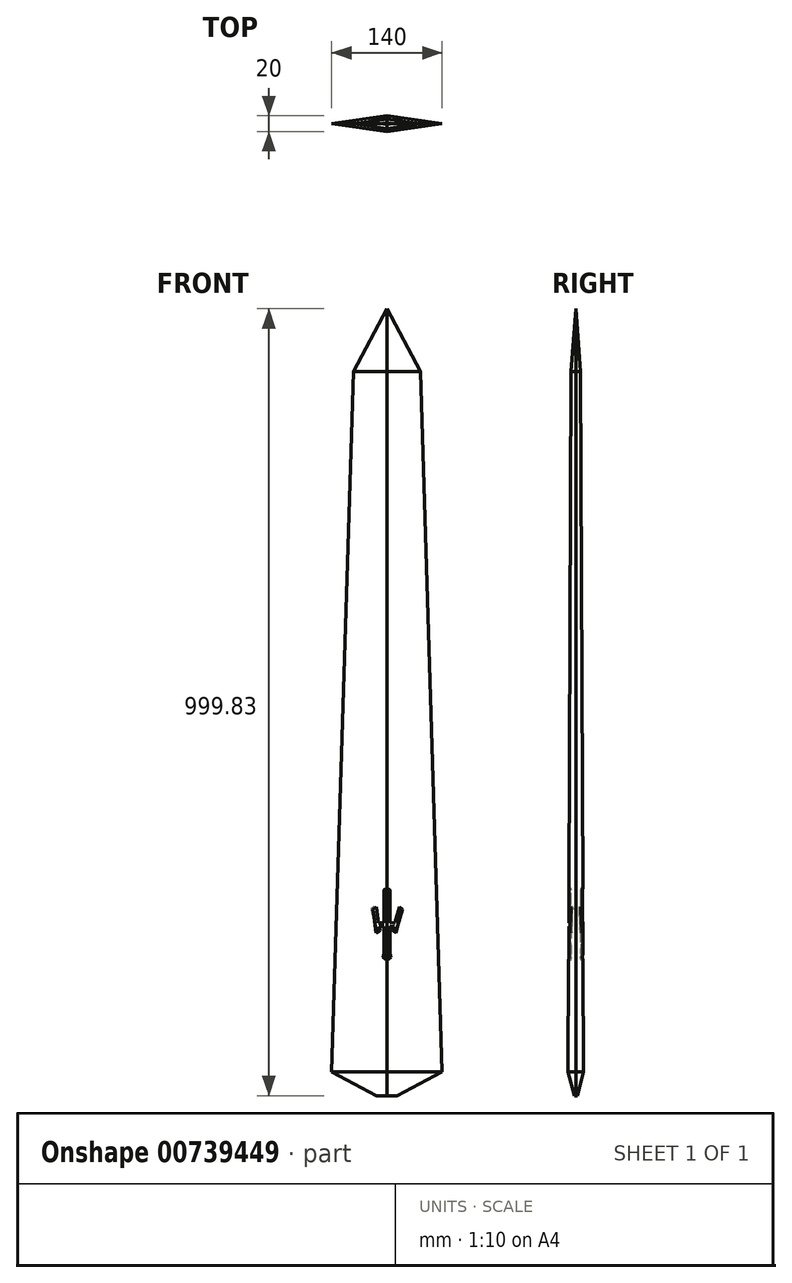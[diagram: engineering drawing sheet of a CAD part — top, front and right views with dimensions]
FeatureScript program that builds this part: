
annotation { "Feature Type Name" : "Feature", "Feature Type Description" : "" }
export const myFeature = defineFeature(function(context is Context, id is Id, definition is map)
    precondition{}
    {
        {
            var Q0;
            Q0=qCreatedBy(makeId("Top.planeOp"),FACE);
            var sketch = newSketch(context, id + "F0", { "sketchPlane" : qUnion([Q0])});
            skLineSegment(sketch, "E0", {"start": v(0, 0) * mm, "end": v(-70, 0) * mm});
            skLineSegment(sketch, "E1", {"start": v(0, 0) * mm, "end": v(70, 0) * mm});
            skLineSegment(sketch, "E2", {"start": v(0, 0) * mm, "end": v(0, 10) * mm});
            skLineSegment(sketch, "E3", {"start": v(0, 0) * mm, "end": v(0, -10) * mm});
            skLineSegment(sketch, "E4", {"start": v(-70, 0) * mm, "end": v(0, 10) * mm});
            skLineSegment(sketch, "E5", {"start": v(70, 0) * mm, "end": v(0, 10) * mm});
            skLineSegment(sketch, "E6", {"start": v(-70, 0) * mm, "end": v(0, -10) * mm});
            skLineSegment(sketch, "E7", {"start": v(70, 0) * mm, "end": v(0, -10) * mm});
            skSolve(sketch);
        }
        {
            var Q0;
            Q0=makeQuery(id+"F0.imprint","IMPRINT",FACE,{"disambiguationData":[TD([[makeQuery(id+"F0.imprint","IMPRINT",EDGE,{"derivedFrom":sQuery(id+"F0.wireOp",EDGE,"E0")}),-1.0]])]});
            var Q1;
            Q1=makeQuery(id+"F0.imprint","IMPRINT",FACE,{"disambiguationData":[TD([[makeQuery(id+"F0.imprint","IMPRINT",EDGE,{"derivedFrom":sQuery(id+"F0.wireOp",EDGE,"E0")}),1.0]])]});
            var Q2;
            Q2=makeQuery(id+"F0.imprint","IMPRINT",FACE,{"disambiguationData":[TD([[makeQuery(id+"F0.imprint","IMPRINT",EDGE,{"derivedFrom":sQuery(id+"F0.wireOp",EDGE,"E1")}),1.0]])]});
            var Q3;
            Q3=makeQuery(id+"F0.imprint","IMPRINT",FACE,{"disambiguationData":[TD([[makeQuery(id+"F0.imprint","IMPRINT",EDGE,{"derivedFrom":sQuery(id+"F0.wireOp",EDGE,"E1")}),-1.0]])]});
            extrude(context, id + "F1", {"entities" : qUnion([Q0, Q1, Q2, Q3]), "depth" : 890 * mm, "offsetDistance" : 25 * mm, "hasDraft" : true, "draftAngle" : .25 * degree, "draftPullDirection" : true});
        }
        {
            var Q0;
            Q0=makeQuery(id+"F1.opExtrude","CAP_FACE",FACE,{"disambiguationData":[OSD([sQuery(id+"F0.wireOp",EDGE,"E4"),sQuery(id+"F0.wireOp",EDGE,"E5"),sQuery(id+"F0.wireOp",EDGE,"E6"),sQuery(id+"F0.wireOp",EDGE,"E7")])],"isStart":false});
            var sketch = newSketch(context, id + "F2", { "sketchPlane" : qUnion([Q0])});
            skSolve(sketch);
        }
        {
            var Q0;
            Q0 = qSketchRegion(id + "F2", true);
            var Q1;
            Q1=makeQuery(id+"F2.imprint","IMPRINT",FACE,{"disambiguationData":[TD([[makeQuery(id+"F2.imprint","IMPRINT",EDGE,{"derivedFrom":makeQuery(id+"F1.opExtrude","CAP_EDGE",EDGE,{"disambiguationData":[OSD([sQuery(id+"F0.wireOp",EDGE,"E4")])],"isStart":false})}),-1.0]])]});
            extrude(context, id + "F3", {"entities" : qUnion([Q0, Q1]), "depth" : 80 * mm, "offsetDistance" : 25 * mm, "hasDraft" : true, "draftAngle" : 4.3 * degree, "draftPullDirection" : true});
        }
        {
            var Q0;
            Q0=makeQuery(id+"F1.opExtrude","CAP_FACE",FACE,{"disambiguationData":[OSD([sQuery(id+"F0.wireOp",EDGE,"E4"),sQuery(id+"F0.wireOp",EDGE,"E5"),sQuery(id+"F0.wireOp",EDGE,"E6"),sQuery(id+"F0.wireOp",EDGE,"E7")])],"isStart":true});
            extrude(context, id + "F4", {"entities" : qUnion([Q0]), "depth" : 30 * mm, "offsetDistance" : 25 * mm, "hasDraft" : true, "draftAngle" : 15 * degree, "draftPullDirection" : true});
        }
        {
            var Q0;
            Q0=makeQuery(id+"F1.opExtrude","SWEPT_FACE",FACE,{"disambiguationData":[OSD([sQuery(id+"F0.wireOp",EDGE,"E6")])]});
            var sketch = newSketch(context, id + "F5", { "sketchPlane" : qUnion([Q0])});
            skLineSegment(sketch, "E8", {"start": v(-2.59, 149.93) * mm, "end": v(1.41, 149.93) * mm});
            skLineSegment(sketch, "E9", {"start": v(-2.59, 231.66) * mm, "end": v(1.41, 231.66) * mm});
            skLineSegment(sketch, "E10", {"start": v(1.41, 231.66) * mm, "end": v(1.41, 149.93) * mm});
            skLineSegment(sketch, "E11", {"start": v(-2.59, 149.93) * mm, "end": v(-2.59, 184.78) * mm});
            skLineSegment(sketch, "E12", {"start": v(-2.59, 184.78) * mm, "end": v(-8.43, 184.78) * mm});
            skLineSegment(sketch, "E13", {"start": v(-8.43, 184.78) * mm, "end": v(-13.43, 184.78) * mm});
            skLineSegment(sketch, "E14", {"start": v(-12.29, 176.83) * mm, "end": v(-13.43, 184.78) * mm});
            skLineSegment(sketch, "E15", {"start": v(-8.43, 184.78) * mm, "end": v(-11.6, 206.86) * mm});
            skLineSegment(sketch, "E16", {"start": v(-13.43, 184.78) * mm, "end": v(-16.6, 206.86) * mm});
            skLineSegment(sketch, "E17", {"start": v(-2.59, 184.78) * mm, "end": v(-2.59, 189.78) * mm});
            skLineSegment(sketch, "E18", {"start": v(-2.59, 189.78) * mm, "end": v(-9.14, 189.78) * mm});
            skLineSegment(sketch, "E19", {"start": v(-2.59, 189.78) * mm, "end": v(-2.59, 231.66) * mm});
            skLineSegment(sketch, "E20", {"start": v(-11.6, 206.86) * mm, "end": v(-12.02, 209.86) * mm});
            skLineSegment(sketch, "E21", {"start": v(-12.02, 209.86) * mm, "end": v(-16.6, 206.86) * mm});
            skLineSegment(sketch, "E22", {"start": v(-7.66, 179.83) * mm, "end": v(-12.29, 176.83) * mm});
            skLineSegment(sketch, "E23", {"start": v(-7.66, 179.83) * mm, "end": v(-8.43, 184.78) * mm});
            skLineSegment(sketch, "E24", {"start": v(1.41, 231.66) * mm, "end": v(1.41, 233.66) * mm});
            skLineSegment(sketch, "E25", {"start": v(1.41, 233.66) * mm, "end": v(-2.59, 231.66) * mm});
            skLineSegment(sketch, "E26", {"start": v(1.41, 149.93) * mm, "end": v(1.41, 141.93) * mm});
            skLineSegment(sketch, "E27", {"start": v(1.41, 145.93) * mm, "end": v(-3.59, 145.93) * mm});
            skLineSegment(sketch, "E28", {"start": v(-3.59, 145.93) * mm, "end": v(-2.59, 149.93) * mm});
            skLineSegment(sketch, "E29", {"start": v(-3.59, 145.93) * mm, "end": v(1.41, 141.93) * mm});
            skSolve(sketch);
        }
        {
            var Q0;
            Q0=makeQuery(id+"F1.opExtrude","SWEPT_FACE",FACE,{"disambiguationData":[OSD([sQuery(id+"F0.wireOp",EDGE,"E7")])]});
            var sketch = newSketch(context, id + "F6", { "sketchPlane" : qUnion([Q0])});
            skLineSegment(sketch, "E30", {"start": v(-1.41, 149.96) * mm, "end": v(2.59, 149.96) * mm});
            skLineSegment(sketch, "E31", {"start": v(2.38, 231.66) * mm, "end": v(-1.41, 231.66) * mm});
            skLineSegment(sketch, "E32", {"start": v(-1.41, 231.66) * mm, "end": v(-1.41, 149.96) * mm});
            skLineSegment(sketch, "E33", {"start": v(2.45, 184.8) * mm, "end": v(2.43, 189.8) * mm});
            skLineSegment(sketch, "E34", {"start": v(10.17, 176.86) * mm, "end": v(12.45, 184.8) * mm});
            skLineSegment(sketch, "E35", {"start": v(2.43, 189.8) * mm, "end": v(8.9, 189.83) * mm});
            skLineSegment(sketch, "E36", {"start": v(7.45, 184.8) * mm, "end": v(8.9, 189.83) * mm});
            skLineSegment(sketch, "E37", {"start": v(12.45, 184.8) * mm, "end": v(18.87, 206.89) * mm});
            skLineSegment(sketch, "E38", {"start": v(2.43, 189.8) * mm, "end": v(2.38, 231.66) * mm});
            skLineSegment(sketch, "E39", {"start": v(2.45, 184.8) * mm, "end": v(2.59, 149.96) * mm});
            skLineSegment(sketch, "E40", {"start": v(7.45, 184.8) * mm, "end": v(12.45, 184.8) * mm});
            skLineSegment(sketch, "E41", {"start": v(7.45, 184.8) * mm, "end": v(2.45, 184.8) * mm});
            skLineSegment(sketch, "E42", {"start": v(6, 179.76) * mm, "end": v(10.17, 176.86) * mm});
            skLineSegment(sketch, "E43", {"start": v(7.45, 184.8) * mm, "end": v(6, 179.76) * mm});
            skLineSegment(sketch, "E44", {"start": v(8.9, 189.83) * mm, "end": v(13.85, 206.89) * mm});
            skLineSegment(sketch, "E45", {"start": v(13.85, 206.89) * mm, "end": v(14.68, 209.76) * mm});
            skLineSegment(sketch, "E46", {"start": v(14.68, 209.76) * mm, "end": v(18.87, 206.89) * mm});
            skLineSegment(sketch, "E47", {"start": v(-1.41, 231.66) * mm, "end": v(-1.41, 233.66) * mm});
            skLineSegment(sketch, "E48", {"start": v(-1.41, 233.66) * mm, "end": v(2.38, 231.66) * mm});
            skLineSegment(sketch, "E49", {"start": v(-1.41, 149.96) * mm, "end": v(-1.41, 141.96) * mm});
            skLineSegment(sketch, "E50", {"start": v(-1.41, 145.96) * mm, "end": v(3.59, 145.96) * mm});
            skLineSegment(sketch, "E51", {"start": v(3.59, 145.96) * mm, "end": v(2.59, 149.96) * mm});
            skLineSegment(sketch, "E52", {"start": v(3.59, 145.96) * mm, "end": v(-1.41, 141.96) * mm});
            skLineSegment(sketch, "E53", {"start": v(6, 179.76) * mm, "end": v(11, 179.76) * mm});
            skSolve(sketch);
        }
        {
            var Q0;
            {var subQ3=sQuery(id+"F5.wireOp",EDGE,"E13");Q0=makeQuery(id+"F5.imprint","IMPRINT",FACE,{"disambiguationData":[TD([[makeQuery(id+"F5.imprint","IMPRINT",EDGE,{"derivedFrom":subQ3}),-1.0]])]});}
            var Q1;
            Q1=makeQuery(id+"F5.imprint","IMPRINT",FACE,{"disambiguationData":[TD([[makeQuery(id+"F5.imprint","IMPRINT",EDGE,{"derivedFrom":sQuery(id+"F5.wireOp",EDGE,"E13")}),1.0]])]});
            var Q2;
            {var subQ0=sQuery(id+"F5.wireOp",EDGE,"E12");Q2=makeQuery(id+"F5.imprint","IMPRINT",FACE,{"disambiguationData":[TD([[makeQuery(id+"F5.imprint","IMPRINT",EDGE,{"derivedFrom":subQ0}),-1.0]])]});}
            var Q3;
            Q3=makeQuery(id+"F5.imprint","IMPRINT",FACE,{"disambiguationData":[TD([[makeQuery(id+"F5.imprint","IMPRINT",EDGE,{"derivedFrom":sQuery(id+"F5.wireOp",EDGE,"E8")}),1.0]])]});
            var Q4;
            Q4=makeQuery(id+"F6.imprint","IMPRINT",FACE,{"disambiguationData":[TD([[makeQuery(id+"F6.imprint","IMPRINT",EDGE,{"derivedFrom":sQuery(id+"F6.wireOp",EDGE,"E30")}),1.0]])]});
            var Q5;
            Q5=makeQuery(id+"F5.imprint","IMPRINT",FACE,{"disambiguationData":[TD([[makeQuery(id+"F5.imprint","IMPRINT",EDGE,{"derivedFrom":sQuery(id+"F5.wireOp",EDGE,"E9")}),1.0]])]});
            var Q6;
            Q6=makeQuery(id+"F6.imprint","IMPRINT",FACE,{"disambiguationData":[TD([[makeQuery(id+"F6.imprint","IMPRINT",EDGE,{"derivedFrom":sQuery(id+"F6.wireOp",EDGE,"E31")}),-1.0]])]});
            var Q7;
            Q7=makeQuery(id+"F6.imprint","IMPRINT",FACE,{"disambiguationData":[TD([[makeQuery(id+"F6.imprint","IMPRINT",EDGE,{"derivedFrom":sQuery(id+"F6.wireOp",EDGE,"E33")}),-1.0]])]});
            var Q8;
            Q8=makeQuery(id+"F6.imprint","IMPRINT",FACE,{"disambiguationData":[TD([[makeQuery(id+"F6.imprint","IMPRINT",EDGE,{"derivedFrom":sQuery(id+"F6.wireOp",EDGE,"E36")}),-1.0]])]});
            var Q9;
            Q9=makeQuery(id+"F6.imprint","IMPRINT",FACE,{"disambiguationData":[TD([[makeQuery(id+"F6.imprint","IMPRINT",EDGE,{"derivedFrom":sQuery(id+"F6.wireOp",EDGE,"E34")}),1.0]])]});
            var Q10;
            {var subQ0=sQuery(id+"F5.wireOp",EDGE,"E8");Q10=makeQuery(id+"F5.imprint","IMPRINT",FACE,{"disambiguationData":[TD([[makeQuery(id+"F5.imprint","IMPRINT",EDGE,{"derivedFrom":subQ0}),-1.0]])]});}
            var Q11;
            {var subQ0=sQuery(id+"F6.wireOp",EDGE,"E30");Q11=makeQuery(id+"F6.imprint","IMPRINT",FACE,{"disambiguationData":[TD([[makeQuery(id+"F6.imprint","IMPRINT",EDGE,{"derivedFrom":subQ0}),-1.0]])]});}
            var Q12;
            {var subQ2=sQuery(id+"F6.wireOp",EDGE,"E50");Q12=makeQuery(id+"F6.imprint","IMPRINT",FACE,{"disambiguationData":[TD([[makeQuery(id+"F6.imprint","IMPRINT",EDGE,{"derivedFrom":subQ2}),-1.0]])]});}
            var Q13;
            {var subQ2=sQuery(id+"F5.wireOp",EDGE,"E27");Q13=makeQuery(id+"F5.imprint","IMPRINT",FACE,{"disambiguationData":[TD([[makeQuery(id+"F5.imprint","IMPRINT",EDGE,{"derivedFrom":subQ2}),1.0]])]});}
            var Q14;
            {var subQ0=sQuery(id+"F6.wireOp",EDGE,"E40");Q14=makeQuery(id+"F6.imprint","IMPRINT",FACE,{"disambiguationData":[TD([[makeQuery(id+"F6.imprint","IMPRINT",EDGE,{"derivedFrom":subQ0}),-1.0]])]});}
            extrude(context, id + "F7", {"entities" : qUnion([Q0, Q1, Q2, Q3, Q4, Q5, Q6, Q7, Q8, Q9, Q10, Q11, Q12, Q13, Q14]), "operationType" : NewBodyOperationType.REMOVE, "oppositeDirection" : true, "depth" : 2.5 * mm, "offsetDistance" : 25 * mm});
        }
        {
            var Q0;
            Q0=makeQuery(id+"F1.opExtrude","SWEPT_FACE",FACE,{"disambiguationData":[OSD([sQuery(id+"F0.wireOp",EDGE,"E5")])]});
            var sketch = newSketch(context, id + "F8", { "sketchPlane" : qUnion([Q0])});
            skLineSegment(sketch, "E54", {"start": v(1.41, 0) * mm, "end": v(1.41, 150) * mm});
            skLineSegment(sketch, "E55", {"start": v(1.41, 150) * mm, "end": v(1.41, 142) * mm});
            skLineSegment(sketch, "E56", {"start": v(1.41, 146) * mm, "end": v(-3.59, 146) * mm});
            skLineSegment(sketch, "E57", {"start": v(1.41, 142) * mm, "end": v(-3.59, 146) * mm});
            skLineSegment(sketch, "E58", {"start": v(1.41, 150) * mm, "end": v(1.41, 231.73) * mm});
            skLineSegment(sketch, "E59", {"start": v(1.41, 231.73) * mm, "end": v(1.41, 233.73) * mm});
            skLineSegment(sketch, "E60", {"start": v(1.41, 231.73) * mm, "end": v(-2.59, 231.73) * mm});
            skLineSegment(sketch, "E61", {"start": v(1.41, 233.73) * mm, "end": v(-2.59, 231.73) * mm});
            skLineSegment(sketch, "E62", {"start": v(-2.59, 231.73) * mm, "end": v(-2.59, 150) * mm});
            skLineSegment(sketch, "E63", {"start": v(-2.59, 150) * mm, "end": v(-3.59, 146) * mm});
            skLineSegment(sketch, "E64", {"start": v(-2.59, 150) * mm, "end": v(1.41, 150) * mm});
            skLineSegment(sketch, "E65", {"start": v(-2.59, 150) * mm, "end": v(-2.59, 184.85) * mm});
            skLineSegment(sketch, "E66", {"start": v(-2.59, 184.85) * mm, "end": v(-2.59, 189.85) * mm});
            skLineSegment(sketch, "E67", {"start": v(-2.59, 184.85) * mm, "end": v(-7.59, 184.85) * mm});
            skLineSegment(sketch, "E68", {"start": v(-7.59, 184.85) * mm, "end": v(-12.59, 184.85) * mm});
            skLineSegment(sketch, "E69", {"start": v(-2.59, 189.85) * mm, "end": v(-9.05, 189.85) * mm});
            skLineSegment(sketch, "E70", {"start": v(-7.59, 184.85) * mm, "end": v(-13.74, 206.73) * mm});
            skLineSegment(sketch, "E71", {"start": v(-13.74, 206.73) * mm, "end": v(-18.74, 206.73) * mm});
            skLineSegment(sketch, "E72", {"start": v(-18.74, 206.73) * mm, "end": v(-12.59, 184.85) * mm});
            skLineSegment(sketch, "E73", {"start": v(-13.74, 206.73) * mm, "end": v(-14.56, 209.63) * mm});
            skLineSegment(sketch, "E74", {"start": v(-14.56, 209.63) * mm, "end": v(-18.74, 206.73) * mm});
            skLineSegment(sketch, "E75", {"start": v(-12.59, 184.85) * mm, "end": v(-10.34, 176.86) * mm});
            skLineSegment(sketch, "E76", {"start": v(-7.59, 184.85) * mm, "end": v(-6.17, 179.8) * mm});
            skLineSegment(sketch, "E77", {"start": v(-6.17, 179.8) * mm, "end": v(-11.17, 179.8) * mm});
            skLineSegment(sketch, "E78", {"start": v(-6.17, 179.8) * mm, "end": v(-10.34, 176.86) * mm});
            skSolve(sketch);
        }
        {
            var Q0;
            Q0=makeQuery(id+"F1.opExtrude","SWEPT_FACE",FACE,{"disambiguationData":[OSD([sQuery(id+"F0.wireOp",EDGE,"E4")])]});
            var sketch = newSketch(context, id + "F9", { "sketchPlane" : qUnion([Q0])});
            skLineSegment(sketch, "E79", {"start": v(-1.41, 150) * mm, "end": v(-1.41, 142) * mm});
            skLineSegment(sketch, "E80", {"start": v(-1.41, 150) * mm, "end": v(-1.41, 231.73) * mm});
            skLineSegment(sketch, "E81", {"start": v(-1.41, 231.73) * mm, "end": v(-1.41, 233.73) * mm});
            skLineSegment(sketch, "E82.MirrorCS", {"start": v(-1.41, 233.73) * mm, "end": v(2.59, 231.73) * mm});
            skLineSegment(sketch, "E83.MirrorCS", {"start": v(-1.41, 231.73) * mm, "end": v(2.59, 231.73) * mm});
            skLineSegment(sketch, "E84.MirrorCS", {"start": v(2.59, 231.73) * mm, "end": v(2.59, 150) * mm});
            skLineSegment(sketch, "E85.MirrorCS", {"start": v(2.59, 189.85) * mm, "end": v(9.05, 189.85) * mm});
            skLineSegment(sketch, "E86.MirrorCS", {"start": v(2.59, 184.85) * mm, "end": v(7.59, 184.85) * mm});
            skLineSegment(sketch, "E87.MirrorCS", {"start": v(6.17, 179.8) * mm, "end": v(10.34, 176.86) * mm});
            skLineSegment(sketch, "E88.MirrorCS", {"start": v(12.59, 184.85) * mm, "end": v(10.34, 176.86) * mm});
            skLineSegment(sketch, "E89.MirrorCS", {"start": v(6.17, 179.8) * mm, "end": v(11.17, 179.8) * mm});
            skLineSegment(sketch, "E90.MirrorCS", {"start": v(7.59, 184.85) * mm, "end": v(6.17, 179.8) * mm});
            skLineSegment(sketch, "E91.MirrorCS", {"start": v(7.59, 184.85) * mm, "end": v(12.59, 184.85) * mm});
            skLineSegment(sketch, "E92.MirrorCS", {"start": v(18.74, 206.73) * mm, "end": v(12.59, 184.85) * mm});
            skLineSegment(sketch, "E93.MirrorCS", {"start": v(7.59, 184.85) * mm, "end": v(13.74, 206.73) * mm});
            skLineSegment(sketch, "E94", {"start": v(13.74, 206.73) * mm, "end": v(18.74, 206.73) * mm});
            skLineSegment(sketch, "E95", {"start": v(13.74, 206.73) * mm, "end": v(14.55, 209.61) * mm});
            skLineSegment(sketch, "E96", {"start": v(14.55, 209.61) * mm, "end": v(18.74, 206.73) * mm});
            skLineSegment(sketch, "E97", {"start": v(-1.41, 146) * mm, "end": v(3.59, 146) * mm});
            skLineSegment(sketch, "E98", {"start": v(2.59, 150) * mm, "end": v(3.59, 146) * mm});
            skLineSegment(sketch, "E99", {"start": v(3.59, 146) * mm, "end": v(-1.41, 142) * mm});
            skLineSegment(sketch, "E100.0.0", {"start": v(-1.41, -0.04) * mm, "end": v(69.3, 0) * mm});
            skLineSegment(sketch, "E100.0.1", {"start": v(41.56, 890) * mm, "end": v(69.3, 0) * mm});
            skLineSegment(sketch, "E100.0.2", {"start": v(41.56, 890) * mm, "end": v(-1.41, 889.96) * mm});
            skLineSegment(sketch, "E100.0.3", {"start": v(-1.41, 889.96) * mm, "end": v(-1.41, -0.04) * mm});
            skLineSegment(sketch, "E101", {"start": v(69.3, 0) * mm, "end": v(-1.41, -0.04) * mm});
            skSolve(sketch);
        }
        {
            var Q0;
            Q0=makeQuery(id+"F8.imprint","IMPRINT",FACE,{"disambiguationData":[TD([[makeQuery(id+"F8.imprint","IMPRINT",EDGE,{"derivedFrom":sQuery(id+"F8.wireOp",EDGE,"E71")}),-1.0]])]});
            var Q1;
            {var subQ3=sQuery(id+"F8.wireOp",EDGE,"E68");Q1=makeQuery(id+"F8.imprint","IMPRINT",FACE,{"disambiguationData":[TD([[makeQuery(id+"F8.imprint","IMPRINT",EDGE,{"derivedFrom":subQ3}),-1.0]])]});}
            var Q2;
            {var subQ0=sQuery(id+"F8.wireOp",EDGE,"E68");Q2=makeQuery(id+"F8.imprint","IMPRINT",FACE,{"disambiguationData":[TD([[makeQuery(id+"F8.imprint","IMPRINT",EDGE,{"derivedFrom":subQ0}),1.0]])]});}
            var Q3;
            {var subQ2=sQuery(id+"F8.wireOp",EDGE,"E77");Q3=makeQuery(id+"F8.imprint","IMPRINT",FACE,{"disambiguationData":[TD([[makeQuery(id+"F8.imprint","IMPRINT",EDGE,{"derivedFrom":subQ2}),1.0]])]});}
            var Q4;
            {var subQ0=sQuery(id+"F8.wireOp",EDGE,"E66");Q4=makeQuery(id+"F8.imprint","IMPRINT",FACE,{"disambiguationData":[TD([[makeQuery(id+"F8.imprint","IMPRINT",EDGE,{"derivedFrom":subQ0}),1.0]])]});}
            var Q5;
            Q5=makeQuery(id+"F8.imprint","IMPRINT",FACE,{"disambiguationData":[TD([[makeQuery(id+"F8.imprint","IMPRINT",EDGE,{"derivedFrom":sQuery(id+"F8.wireOp",EDGE,"E58")}),-1.0]])]});
            var Q6;
            Q6=makeQuery(id+"F8.imprint","IMPRINT",FACE,{"disambiguationData":[TD([[makeQuery(id+"F8.imprint","IMPRINT",EDGE,{"derivedFrom":sQuery(id+"F8.wireOp",EDGE,"E59")}),-1.0]])]});
            var Q7;
            {var subQ0=sQuery(id+"F9.wireOp",EDGE,"E82.MirrorCS");Q7=makeQuery(id+"F9.imprint","IMPRINT",FACE,{"disambiguationData":[TD([[makeQuery(id+"F9.imprint","IMPRINT",EDGE,{"derivedFrom":subQ0}),-1.0]])]});}
            var Q8;
            {var subQ4=sQuery(id+"F9.wireOp",EDGE,"E83.MirrorCS");Q8=makeQuery(id+"F9.imprint","IMPRINT",FACE,{"disambiguationData":[TD([[makeQuery(id+"F9.imprint","IMPRINT",EDGE,{"derivedFrom":subQ4}),-1.0]])]});}
            var Q9;
            {var subQ0=sQuery(id+"F9.wireOp",EDGE,"E86.MirrorCS");Q9=makeQuery(id+"F9.imprint","IMPRINT",FACE,{"disambiguationData":[TD([[makeQuery(id+"F9.imprint","IMPRINT",EDGE,{"derivedFrom":subQ0}),1.0]])]});}
            var Q10;
            {var subQ3=sQuery(id+"F9.wireOp",EDGE,"E91.MirrorCS");Q10=makeQuery(id+"F9.imprint","IMPRINT",FACE,{"disambiguationData":[TD([[makeQuery(id+"F9.imprint","IMPRINT",EDGE,{"derivedFrom":subQ3}),1.0]])]});}
            var Q11;
            {var subQ2=sQuery(id+"F9.wireOp",EDGE,"E89.MirrorCS");Q11=makeQuery(id+"F9.imprint","IMPRINT",FACE,{"disambiguationData":[TD([[makeQuery(id+"F9.imprint","IMPRINT",EDGE,{"derivedFrom":subQ2}),1.0]])]});}
            var Q12;
            {var subQ0=sQuery(id+"F9.wireOp",EDGE,"E87.MirrorCS");Q12=makeQuery(id+"F9.imprint","IMPRINT",FACE,{"disambiguationData":[TD([[makeQuery(id+"F9.imprint","IMPRINT",EDGE,{"derivedFrom":subQ0}),1.0]])]});}
            var Q13;
            Q13=makeQuery(id+"F9.imprint","IMPRINT",FACE,{"disambiguationData":[TD([[makeQuery(id+"F9.imprint","IMPRINT",EDGE,{"derivedFrom":sQuery(id+"F9.wireOp",EDGE,"E94")}),1.0]])]});
            var Q14;
            {var subQ2=sQuery(id+"F8.wireOp",EDGE,"E56");Q14=makeQuery(id+"F8.imprint","IMPRINT",FACE,{"disambiguationData":[TD([[makeQuery(id+"F8.imprint","IMPRINT",EDGE,{"derivedFrom":subQ2}),1.0]])]});}
            var Q15;
            {var subQ0=sQuery(id+"F9.wireOp",EDGE,"E97");Q15=makeQuery(id+"F9.imprint","IMPRINT",FACE,{"disambiguationData":[TD([[makeQuery(id+"F9.imprint","IMPRINT",EDGE,{"derivedFrom":subQ0}),-1.0]])]});}
            var Q16;
            {var subQ2=sQuery(id+"F8.wireOp",EDGE,"E56");Q16=makeQuery(id+"F8.imprint","IMPRINT",FACE,{"disambiguationData":[TD([[makeQuery(id+"F8.imprint","IMPRINT",EDGE,{"derivedFrom":subQ2}),-1.0]])]});}
            extrude(context, id + "F10", {"entities" : qUnion([Q0, Q1, Q2, Q3, Q4, Q5, Q6, Q7, Q8, Q9, Q10, Q11, Q12, Q13, Q14, Q15, Q16]), "operationType" : NewBodyOperationType.REMOVE, "oppositeDirection" : true, "depth" : 2.5 * mm, "offsetDistance" : 25 * mm});
        }
    });
